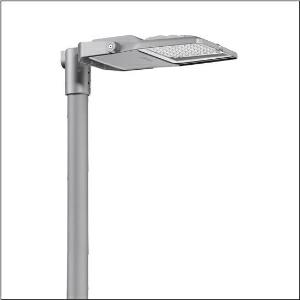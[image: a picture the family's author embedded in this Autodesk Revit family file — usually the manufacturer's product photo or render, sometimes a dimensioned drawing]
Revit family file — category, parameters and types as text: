
# Revit family: floodlight_fl_21_iq_mini___pl64_5xa7771c4e3a_84b6
name_source: partatom
category: Lighting Fixtures
units: mm (PartAtom-declared; Revit-internal decimal feet)

## family parameters
Cut with Voids When Loaded = No
Host = Face
Light Source = No
Part Type = Normal
Room Calculation Point = No
Round Connector Dimension = Use Diameter
Shared = No

## types (1)
- --- (1 x LED, 12280 lm, 87.2 W, 4000K)
    Apparent Load = 87 VA
    CIE Flux Codes = 28 80 98 100 100
    Color Rendering = 70
    Color Temperature = 4000K
    Default Elevation = 1800 mm
    Description = Floodlight FL 21 iQ mini, floodlight, primary light control with lens, of PMMA, primary optical cover: protective disc, of toughened safety glass, transparent, light distribution: PL64, light emission: direct distribution, installation type: surface-mounted, lamps: LED, High Power LED, rated values: 12.280lm | 87,2W | 140,8lm/W (begin service life); end service life: 12.280lm | 92,1W; at 50% lumin. flux: 6.140lm | 40,2W | 152,7lm/W, colour temperature: 4000K, colour rendering: CRI > 70, light colour: 740, light setting 1 begin service life: 100% | 12.280lm | 87,2W | 140,8lm/W | 4.000K, light setting 1 end service life: 92,1W, further light settings possible, control: Auto-Match, Temp-Guard, Lumen-Switch, Night-Set, Smart-Wire, Light-Fading, Desk-Remote (wireless, voltage-free reading and setting of iQ features in the workshop via application-optimized NFC function/RFID function), optimised constant luminous flux control (CLO 2.0), pre-setting: linear dimming characteristic, with terminal, 6-pole, mains connection: 220..240V, AC, 50/60Hz, luminaire housing, of diecast aluminium, powder-coated, SITECO metallic grey (DB 702S), corrosivity category C5 mid according to DIN EN ISO 12944suitable for swimming poolschlorine-resistant, sealing non-destructively replaceable, please order mast flange separately, mast bracket, of steel, galvanised, powder-coated, SITECO metallic grey (DB 702S), protection rating (complete): IP66, insulation class (complete): insulation class II (safety insulation), certification: CE, ENEC, VDE, protection symbol: D, impact resistance: IK08, permissible operating ambient temperature: -40..+40°C, permissible operating ambient temperature for outdoor applications: -40..+50°C, standard: DIN EN 12944, LABS conformity tested according to VDMA 24364:2018-05, packaging unit: 1 piece

Light Distribution: PL64
    Height = 70 mm
    Lamp = 1 x LED
    Lamp Light Flux = 12280 lm
    Lamp Power = 87.2 W
    Lamp count = 1
    Length = 485 mm
    Luminous efficacy = 141 lm/W
    Manufacturer = Siteco
    ModVariant = No
    Model = 5XA7771C4E3A
    Mounting Place = Pole
    Mounting Type = Pole annexe
    Number of Poles = 1
    OnlyDefault = Yes
    Power Factor = 1
    Product Name = Floodlight FL 21 iQ mini | PL64
    Product group = floodlight | pylon annexe
    ProductGroupID = 6201
    Protection Class = Protection class II
    Protection Degree = IP 66
    RLX_Detail_Level = 1
    RLX_Emergency_Light_Flux = 0 lm
    RLX_Emergency_Type = 0
    RLX_Emergency_Type_DB = No
    RlxData = <blob elided: 101605 chars, md5=49e288dc>
    Socket = socket
    Standby Power = 0 W
    System Light Flux = 12280 lm
    System Power = 87 W
    Type Comments = factory setting: luminous flux: 100 % | dim-lin: 254 | 456 mA
    Type Image = l_1007125.jpg
    URL = http://relux.com
    VarID = @adj_167539
    Voltage = 0 V
    Weight = 0.00 kg
    Width = 337 mm

## geometry (parser evidence)
native form markers: Blend x4, Sweep x13
no freeform markers — native parametric forms only
